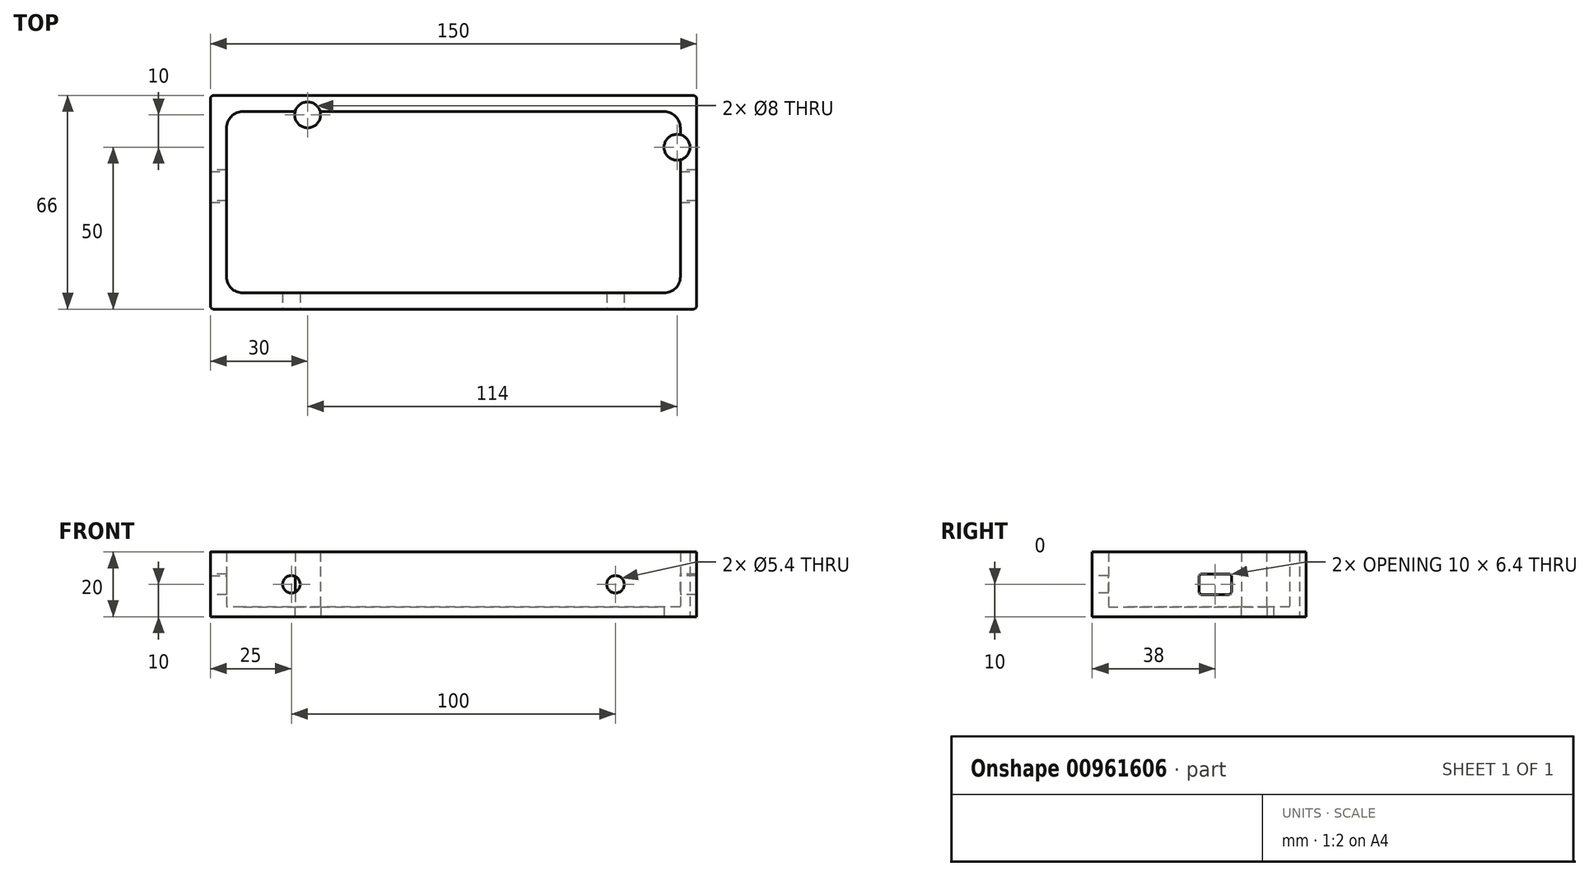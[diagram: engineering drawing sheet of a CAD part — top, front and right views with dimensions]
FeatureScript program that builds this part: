
annotation { "Feature Type Name" : "Feature", "Feature Type Description" : "" }
export const myFeature = defineFeature(function(context is Context, id is Id, definition is map)
    precondition{}
    {
        {
            var Q0;
            Q0=qCreatedBy(makeId("Top.planeOp"),FACE);
            var sketch = newSketch(context, id + "F0", { "sketchPlane" : qUnion([Q0])});
            skLineSegment(sketch, "E0.bottom", {"start": v(-75, 43) * mm, "end": v(75, 43) * mm});
            skLineSegment(sketch, "E0.top", {"start": v(-75, -43) * mm, "end": v(75, -43) * mm});
            skLineSegment(sketch, "E0.left", {"start": v(-75, 43) * mm, "end": v(-75, -43) * mm});
            skLineSegment(sketch, "E0.right", {"start": v(75, 43) * mm, "end": v(75, -43) * mm});
            skCircle(sketch, "E1", {"center": v(-69, -37) * mm, "radius": 2 * mm});
            skCircle(sketch, "E2", {"center": v(69, -37) * mm, "radius": 2 * mm});
            skCircle(sketch, "E3", {"center": v(69, 27) * mm, "radius": 2 * mm});
            skCircle(sketch, "E4", {"center": v(-45, 37) * mm, "radius": 2 * mm});
            skSolve(sketch);
        }
        {
            var Q0;
            Q0=qCreatedBy(makeId("Top.planeOp"),FACE);
            var sketch = newSketch(context, id + "F1", { "sketchPlane" : qUnion([Q0])});
            skLineSegment(sketch, "E5", {"start": v(-75, -23) * mm, "end": v(75, -23) * mm});
            skLineSegment(sketch, "E6", {"start": v(75, -23) * mm, "end": v(75, 43) * mm});
            skLineSegment(sketch, "E7", {"start": v(75, 43) * mm, "end": v(-75, 43) * mm});
            skLineSegment(sketch, "E8", {"start": v(-75, 43) * mm, "end": v(-75, -23) * mm});
            skLineSegment(sketch, "E9", {"start": v(70, 38) * mm, "end": v(70, -18) * mm});
            skLineSegment(sketch, "E10", {"start": v(70, -18) * mm, "end": v(-70, -18) * mm});
            skLineSegment(sketch, "E11", {"start": v(-70, -18) * mm, "end": v(-70, 38) * mm});
            skLineSegment(sketch, "E12", {"start": v(-70, 38) * mm, "end": v(70, 38) * mm});
            skArc(sketch, "E13", {"start": v(70, 20.07) * mm, "mid": v(64.42, 21.7) * mm, "end": v(62, 27) * mm});
            skLineSegment(sketch, "E14", {"start": v(62, 27) * mm, "end": v(62, 38) * mm});
            skArc(sketch, "E15", {"start": v(-38.07, 38) * mm, "mid": v(-39.7, 32.42) * mm, "end": v(-45, 30) * mm});
            skLineSegment(sketch, "E16", {"start": v(-45, 30) * mm, "end": v(-70, 30) * mm});
            skCircle(sketch, "E17", {"center": v(69, 27) * mm, "radius": 4 * mm});
            skCircle(sketch, "E18", {"center": v(-45, 37) * mm, "radius": 4 * mm});
            skCircle(sketch, "E19", {"center": v(-45, 37) * mm, "radius": 2 * mm});
            skCircle(sketch, "E20", {"center": v(69, 27) * mm, "radius": 2 * mm});
            skLineSegment(sketch, "E21", {"start": v(-70, -13) * mm, "end": v(-65, -18) * mm});
            skLineSegment(sketch, "E22", {"start": v(65, -18) * mm, "end": v(70, -13) * mm});
            skSolve(sketch);
        }
        {
            var Q0;
            Q0=makeQuery(id+"F1.imprint","IMPRINT",FACE,{"disambiguationData":[TD([[makeQuery(id+"F1.imprint","IMPRINT",EDGE,{"derivedFrom":sQuery(id+"F1.wireOp",EDGE,"E5")}),1.0]])]});
            extrude(context, id + "F2", {"entities" : qUnion([Q0]), "depth" : 20 * mm, "offsetDistance" : 25 * mm});
        }
        {
            var Q0;
            {var subQ5=sQuery(id+"F1.wireOp",EDGE,"E15");Q0=makeQuery(id+"F1.imprint","IMPRINT",FACE,{"disambiguationData":[TD([[makeQuery(id+"F1.imprint","IMPRINT",EDGE,{"derivedFrom":subQ5}),-1.0]])]});}
            var Q1;
            {var subQ0=sQuery(id+"F1.wireOp",EDGE,"E13");Q1=makeQuery(id+"F1.imprint","IMPRINT",FACE,{"disambiguationData":[TD([[makeQuery(id+"F1.imprint","IMPRINT",EDGE,{"derivedFrom":subQ0}),-1.0]])]});}
            var Q2;
            {var subQ0=sQuery(id+"F1.wireOp",EDGE,"E17");var subQ1=sQuery(id+"F1.wireOp",EDGE,"E9");var subQ2=makeQuery(id+"F1.imprint","INTERSECT",VERTEX,{"disambiguationData":[OD(0.0)],"derivedFrom":[subQ1,subQ0]});Q2=makeQuery(id+"F1.imprint","IMPRINT",FACE,{"disambiguationData":[TD([[makeQuery(id+"F1.imprint","IMPRINT",EDGE,{"disambiguationData":[TD([[subQ2,-1.0]])],"derivedFrom":subQ1}),1.0]])]});}
            var Q3;
            {var subQ0=sQuery(id+"F1.wireOp",EDGE,"E17");var subQ1=sQuery(id+"F1.wireOp",EDGE,"E9");var subQ2=makeQuery(id+"F1.imprint","INTERSECT",VERTEX,{"disambiguationData":[OD(0.0)],"derivedFrom":[subQ1,subQ0]});Q3=makeQuery(id+"F1.imprint","IMPRINT",FACE,{"disambiguationData":[TD([[makeQuery(id+"F1.imprint","IMPRINT",EDGE,{"disambiguationData":[TD([[subQ2,-1.0]])],"derivedFrom":subQ1}),-1.0]])]});}
            var Q4;
            {var subQ0=sQuery(id+"F1.wireOp",EDGE,"E18");var subQ1=sQuery(id+"F1.wireOp",EDGE,"E12");var subQ2=makeQuery(id+"F1.imprint","INTERSECT",VERTEX,{"disambiguationData":[OD(0.0)],"derivedFrom":[subQ1,subQ0]});Q4=makeQuery(id+"F1.imprint","IMPRINT",FACE,{"disambiguationData":[TD([[makeQuery(id+"F1.imprint","IMPRINT",EDGE,{"disambiguationData":[TD([[subQ2,-1.0]])],"derivedFrom":subQ1}),-1.0]])]});}
            var Q5;
            {var subQ0=sQuery(id+"F1.wireOp",EDGE,"E18");var subQ1=sQuery(id+"F1.wireOp",EDGE,"E12");var subQ2=makeQuery(id+"F1.imprint","INTERSECT",VERTEX,{"disambiguationData":[OD(0.0)],"derivedFrom":[subQ1,subQ0]});Q5=makeQuery(id+"F1.imprint","IMPRINT",FACE,{"disambiguationData":[TD([[makeQuery(id+"F1.imprint","IMPRINT",EDGE,{"disambiguationData":[TD([[subQ2,-1.0]])],"derivedFrom":subQ1}),1.0]])]});}
            var Q6;
            {var subQ3=sQuery(id+"F1.wireOp",EDGE,"E21");Q6=makeQuery(id+"F1.imprint","IMPRINT",FACE,{"disambiguationData":[TD([[makeQuery(id+"F1.imprint","IMPRINT",EDGE,{"derivedFrom":subQ3}),-1.0]])]});}
            var Q7;
            {var subQ3=sQuery(id+"F1.wireOp",EDGE,"E22");Q7=makeQuery(id+"F1.imprint","IMPRINT",FACE,{"disambiguationData":[TD([[makeQuery(id+"F1.imprint","IMPRINT",EDGE,{"derivedFrom":subQ3}),-1.0]])]});}
            extrude(context, id + "F3", {"entities" : qUnion([Q0, Q1, Q2, Q3, Q4, Q5, Q6, Q7]), "operationType" : NewBodyOperationType.ADD, "depth" : 3 * mm, "offsetDistance" : 25 * mm});
        }
        {
            var Q0;
            Q0=makeQuery(id+"F2.opExtrude","SWEPT_FACE",FACE,{"disambiguationData":[OSD([sQuery(id+"F1.wireOp",EDGE,"E5")])]});
            var sketch = newSketch(context, id + "F4", { "sketchPlane" : qUnion([Q0])});
            skCircle(sketch, "E23", {"center": v(-50, 10) * mm, "radius": 2.7 * mm});
            skCircle(sketch, "E24", {"center": v(50, 10) * mm, "radius": 2.7 * mm});
            skSolve(sketch);
        }
        {
            var Q0;
            Q0=makeQuery(id+"F2.opExtrude","SWEPT_FACE",FACE,{"disambiguationData":[OSD([sQuery(id+"F1.wireOp",EDGE,"E8")])]});
            var sketch = newSketch(context, id + "F5", { "sketchPlane" : qUnion([Q0])});
            skLineSegment(sketch, "E25.bottom", {"start": v(-20, 6.8) * mm, "end": v(-10, 6.8) * mm});
            skLineSegment(sketch, "E25.top", {"start": v(-20, 13.2) * mm, "end": v(-10, 13.2) * mm});
            skLineSegment(sketch, "E25.left", {"start": v(-10, 13.2) * mm, "end": v(-10, 6.8) * mm});
            skLineSegment(sketch, "E25.right", {"start": v(-20, 13.2) * mm, "end": v(-20, 6.8) * mm});
            skSolve(sketch);
        }
        {
            var Q0;
            Q0=makeQuery(id+"F4.imprint","IMPRINT",FACE,{"disambiguationData":[TD([[makeQuery(id+"F4.imprint","IMPRINT",EDGE,{"derivedFrom":sQuery(id+"F4.wireOp",EDGE,"E23")}),1.0]])]});
            var Q1;
            Q1=makeQuery(id+"F4.imprint","IMPRINT",FACE,{"disambiguationData":[TD([[makeQuery(id+"F4.imprint","IMPRINT",EDGE,{"derivedFrom":sQuery(id+"F4.wireOp",EDGE,"E24")}),1.0]])]});
            extrude(context, id + "F6", {"entities" : qUnion([Q0, Q1]), "operationType" : NewBodyOperationType.REMOVE, "oppositeDirection" : true, "depth" : 25 * mm, "offsetDistance" : 25 * mm});
        }
        {
            var Q0;
            Q0=makeQuery(id+"F5.imprint","IMPRINT",FACE,{"disambiguationData":[TD([[makeQuery(id+"F5.imprint","IMPRINT",EDGE,{"derivedFrom":sQuery(id+"F5.wireOp",EDGE,"E25.bottom")}),1.0]])]});
            extrude(context, id + "F7", {"entities" : qUnion([Q0]), "operationType" : NewBodyOperationType.REMOVE, "oppositeDirection" : true, "depth" : 160 * mm, "offsetDistance" : 25 * mm});
        }
        {
            var Q0;
            Q0=makeQuery(id+"F3.opExtrude","SWEPT_EDGE",EDGE,{"disambiguationData":[OSD([sQuery(id+"F1.wireOp",EDGE,"E12"),sQuery(id+"F1.wireOp",EDGE,"E14")])]});
            var Q1;
            Q1=makeQuery(id+"F3.opExtrude","SWEPT_EDGE",EDGE,{"disambiguationData":[OSD([sQuery(id+"F1.wireOp",EDGE,"E11"),sQuery(id+"F1.wireOp",EDGE,"E16")])]});
            var Q2;
            Q2=makeQuery(id+"F2.opExtrude","SWEPT_EDGE",EDGE,{"disambiguationData":[OSD([sQuery(id+"F1.wireOp",EDGE,"E9"),sQuery(id+"F1.wireOp",EDGE,"E12")])]});
            var Q3;
            Q3=makeQuery(id+"F2.opExtrude","SWEPT_EDGE",EDGE,{"disambiguationData":[OSD([sQuery(id+"F1.wireOp",EDGE,"E11"),sQuery(id+"F1.wireOp",EDGE,"E12")])]});
            var Q4;
            Q4=makeQuery(id+"F2.opExtrude","SWEPT_EDGE",EDGE,{"disambiguationData":[OSD([sQuery(id+"F1.wireOp",EDGE,"E10"),sQuery(id+"F1.wireOp",EDGE,"E11")])]});
            var Q5;
            Q5=makeQuery(id+"F2.opExtrude","SWEPT_EDGE",EDGE,{"disambiguationData":[OSD([sQuery(id+"F1.wireOp",EDGE,"E9"),sQuery(id+"F1.wireOp",EDGE,"E10")])]});
            var Q6;
            Q6=makeQuery(id+"F3.opExtrude","SWEPT_EDGE",EDGE,{"disambiguationData":[OSD([sQuery(id+"F1.wireOp",EDGE,"E12"),sQuery(id+"F1.wireOp",EDGE,"E15")])]});
            var Q7;
            Q7=makeQuery(id+"F3.opExtrude","SWEPT_EDGE",EDGE,{"disambiguationData":[OSD([sQuery(id+"F1.wireOp",EDGE,"E9"),sQuery(id+"F1.wireOp",EDGE,"E13")])]});
            fillet(context, id + "F8", {"entities" : qUnion([Q0, Q1, Q2, Q3, Q4, Q5, Q6, Q7]), "radius" : 5 * mm, "tangentPropagation" : true, "allowEdgeOverflow" : false});
        }
        {
            var Q0;
            Q0=makeQuery(id+"F2.opExtrude","SWEPT_EDGE",EDGE,{"disambiguationData":[OSD([sQuery(id+"F1.wireOp",EDGE,"E7"),sQuery(id+"F1.wireOp",EDGE,"E8")])]});
            var Q1;
            Q1=makeQuery(id+"F2.opExtrude","SWEPT_EDGE",EDGE,{"disambiguationData":[OSD([sQuery(id+"F1.wireOp",EDGE,"E5"),sQuery(id+"F1.wireOp",EDGE,"E8")])]});
            var Q2;
            Q2=makeQuery(id+"F2.opExtrude","SWEPT_EDGE",EDGE,{"disambiguationData":[OSD([sQuery(id+"F1.wireOp",EDGE,"E5"),sQuery(id+"F1.wireOp",EDGE,"E6")])]});
            var Q3;
            Q3=makeQuery(id+"F2.opExtrude","SWEPT_EDGE",EDGE,{"disambiguationData":[OSD([sQuery(id+"F1.wireOp",EDGE,"E6"),sQuery(id+"F1.wireOp",EDGE,"E7")])]});
            var Q4;
            {var subQ0=sQuery(id+"F5.wireOp",EDGE,"E25.bottom");var subQ1=sQuery(id+"F5.wireOp",EDGE,"E25.left");Q4=makeQuery(id+"F7.boolean.opBoolean","COPY",EDGE,{"disambiguationData":[TD([makeQuery(id+"F2.opExtrude","SWEPT_FACE",FACE,{"disambiguationData":[OSD([sQuery(id+"F1.wireOp",EDGE,"E8")])]})])],"derivedFrom":makeQuery(id+"F7.opExtrude","SWEPT_EDGE",EDGE,{"disambiguationData":[OSD([subQ0,subQ1])]})});}
            var Q5;
            {var subQ0=sQuery(id+"F5.wireOp",EDGE,"E25.bottom");var subQ1=sQuery(id+"F5.wireOp",EDGE,"E25.right");Q5=makeQuery(id+"F7.boolean.opBoolean","COPY",EDGE,{"disambiguationData":[TD([makeQuery(id+"F2.opExtrude","SWEPT_FACE",FACE,{"disambiguationData":[OSD([sQuery(id+"F1.wireOp",EDGE,"E8")])]})])],"derivedFrom":makeQuery(id+"F7.opExtrude","SWEPT_EDGE",EDGE,{"disambiguationData":[OSD([subQ0,subQ1])]})});}
            var Q6;
            {var subQ3=sQuery(id+"F5.wireOp",EDGE,"E25.bottom");var subQ4=sQuery(id+"F5.wireOp",EDGE,"E25.right");Q6=makeQuery(id+"F7.boolean.opBoolean","COPY",EDGE,{"disambiguationData":[TD([makeQuery(id+"F2.opExtrude","SWEPT_FACE",FACE,{"disambiguationData":[OSD([sQuery(id+"F1.wireOp",EDGE,"E6")])]})])],"derivedFrom":makeQuery(id+"F7.opExtrude","SWEPT_EDGE",EDGE,{"disambiguationData":[OSD([subQ3,subQ4])]})});}
            var Q7;
            {var subQ0=sQuery(id+"F5.wireOp",EDGE,"E25.left");var subQ4=sQuery(id+"F5.wireOp",EDGE,"E25.bottom");Q7=makeQuery(id+"F7.boolean.opBoolean","COPY",EDGE,{"disambiguationData":[TD([makeQuery(id+"F2.opExtrude","SWEPT_FACE",FACE,{"disambiguationData":[OSD([sQuery(id+"F1.wireOp",EDGE,"E6")])]})])],"derivedFrom":makeQuery(id+"F7.opExtrude","SWEPT_EDGE",EDGE,{"disambiguationData":[OSD([subQ4,subQ0])]})});}
            fillet(context, id + "F9", {"entities" : qUnion([Q0, Q1, Q2, Q3, Q4, Q5, Q6, Q7]), "radius" : 1 * mm, "tangentPropagation" : true, "allowEdgeOverflow" : false});
        }
        {
            var Q0;
            {var subQ0=sQuery(id+"F5.wireOp",EDGE,"E25.top");var subQ1=sQuery(id+"F5.wireOp",EDGE,"E25.left");Q0=makeQuery(id+"F7.boolean.opBoolean","COPY",EDGE,{"disambiguationData":[TD([makeQuery(id+"F2.opExtrude","SWEPT_FACE",FACE,{"disambiguationData":[OSD([sQuery(id+"F1.wireOp",EDGE,"E8")])]})])],"derivedFrom":makeQuery(id+"F7.opExtrude","SWEPT_EDGE",EDGE,{"disambiguationData":[OSD([subQ0,subQ1])]})});}
            var Q1;
            {var subQ0=sQuery(id+"F5.wireOp",EDGE,"E25.right");var subQ1=sQuery(id+"F5.wireOp",EDGE,"E25.top");Q1=makeQuery(id+"F7.boolean.opBoolean","COPY",EDGE,{"disambiguationData":[TD([makeQuery(id+"F2.opExtrude","SWEPT_FACE",FACE,{"disambiguationData":[OSD([sQuery(id+"F1.wireOp",EDGE,"E8")])]})])],"derivedFrom":makeQuery(id+"F7.opExtrude","SWEPT_EDGE",EDGE,{"disambiguationData":[OSD([subQ1,subQ0])]})});}
            var Q2;
            {var subQ3=sQuery(id+"F5.wireOp",EDGE,"E25.top");var subQ4=sQuery(id+"F5.wireOp",EDGE,"E25.right");Q2=makeQuery(id+"F7.boolean.opBoolean","COPY",EDGE,{"disambiguationData":[TD([makeQuery(id+"F2.opExtrude","SWEPT_FACE",FACE,{"disambiguationData":[OSD([sQuery(id+"F1.wireOp",EDGE,"E6")])]})])],"derivedFrom":makeQuery(id+"F7.opExtrude","SWEPT_EDGE",EDGE,{"disambiguationData":[OSD([subQ3,subQ4])]})});}
            var Q3;
            {var subQ0=sQuery(id+"F5.wireOp",EDGE,"E25.left");var subQ4=sQuery(id+"F5.wireOp",EDGE,"E25.top");Q3=makeQuery(id+"F7.boolean.opBoolean","COPY",EDGE,{"disambiguationData":[TD([makeQuery(id+"F2.opExtrude","SWEPT_FACE",FACE,{"disambiguationData":[OSD([sQuery(id+"F1.wireOp",EDGE,"E6")])]})])],"derivedFrom":makeQuery(id+"F7.opExtrude","SWEPT_EDGE",EDGE,{"disambiguationData":[OSD([subQ4,subQ0])]})});}
            chamfer(context, id + "F10", {"entities" : qUnion([Q0, Q1, Q2, Q3]), "width" : 0.5 * mm, "tangentPropagation" : true});
        }
    });
